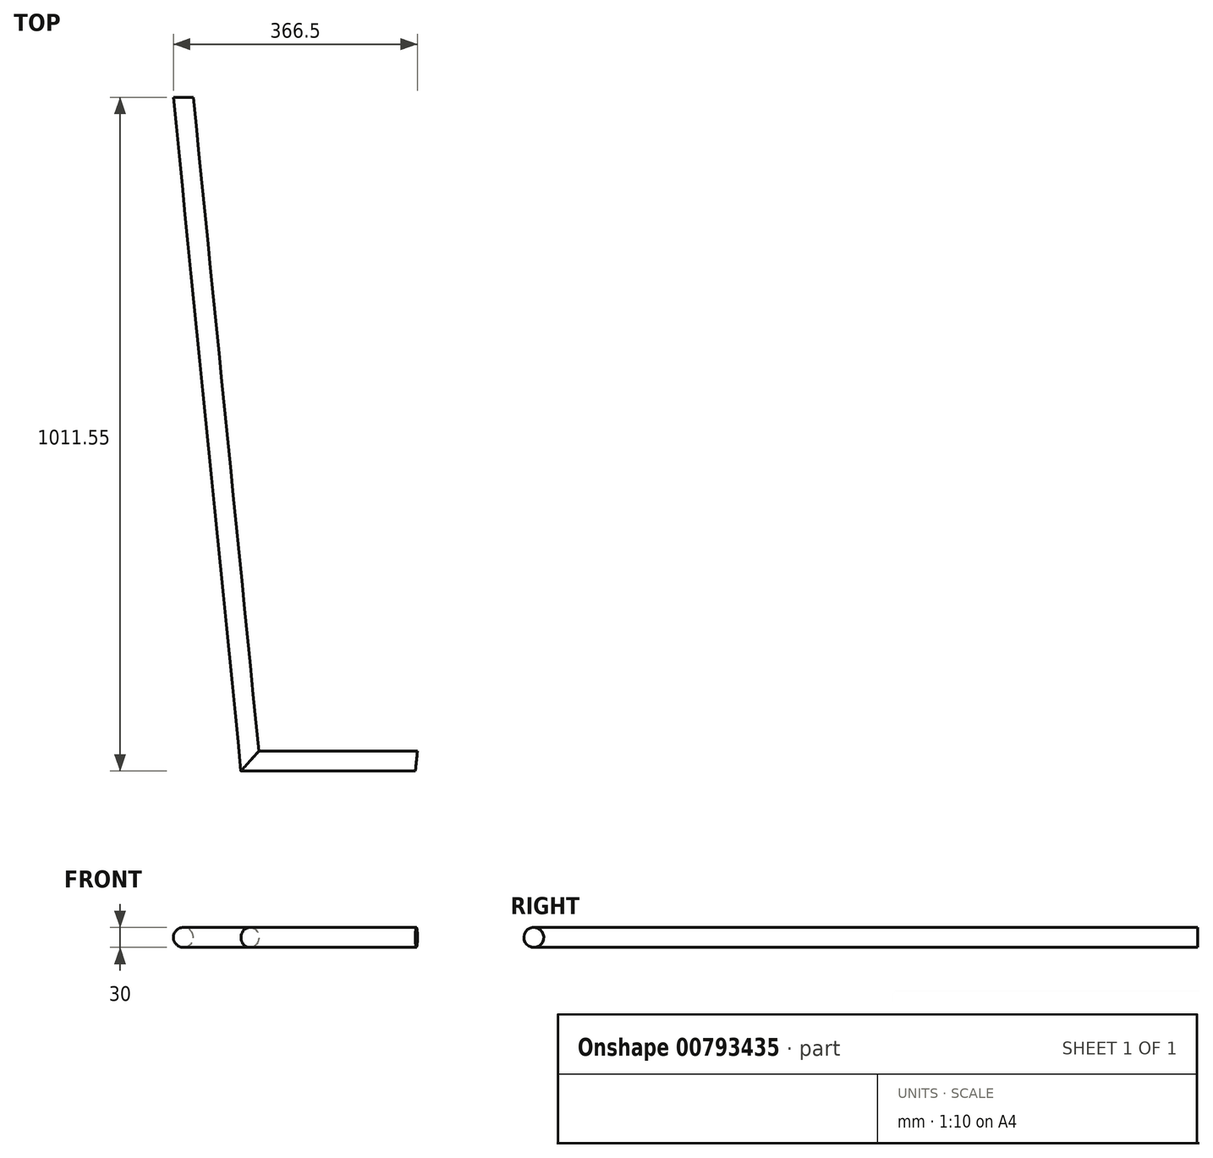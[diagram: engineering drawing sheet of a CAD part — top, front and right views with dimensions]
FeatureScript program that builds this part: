
annotation { "Feature Type Name" : "Feature", "Feature Type Description" : "" }
export const myFeature = defineFeature(function(context is Context, id is Id, definition is map)
    precondition{}
    {
        {
            var Q0;
            Q0=qCreatedBy(makeId("Top.planeOp"),FACE);
            var sketch = newSketch(context, id + "F0", { "sketchPlane" : qUnion([Q0])});
            skLineSegment(sketch, "E0", {"start": v(0, 0) * mm, "end": v(-250, 0) * mm});
            skLineSegment(sketch, "E1", {"start": v(0, -996.63) * mm, "end": v(100, -996.63) * mm});
            skLineSegment(sketch, "E2", {"start": v(100, -996.63) * mm, "end": v(0, 0) * mm});
            skLineSegment(sketch, "E3", {"start": v(100, -996.63) * mm, "end": v(350, -996.63) * mm});
            skLineSegment(sketch, "E4", {"start": v(0, 0) * mm, "end": v(400, 0) * mm});
            skSolve(sketch);
        }
        {
            var Q0;
            Q0=qCreatedBy(makeId("Front.planeOp"),FACE);
            var sketch = newSketch(context, id + "F1", { "sketchPlane" : qUnion([Q0])});
            skCircle(sketch, "E5", {"center": v(0, 0) * mm, "radius": 15 * mm});
            skSolve(sketch);
        }
        {
            var Q0;
            Q0=makeQuery(id+"F1.imprint","IMPRINT",FACE,{"disambiguationData":[TD([[makeQuery(id+"F1.imprint","IMPRINT",EDGE,{"derivedFrom":sQuery(id+"F1.wireOp",EDGE,"E5")}),1.0]])]});
            var Q1;
            Q1=sQuery(id+"F0.wireOp",EDGE,"E2");
            var Q2;
            Q2=sQuery(id+"F0.wireOp",EDGE,"E3");
            sweep(context, id + "F2", {"profiles" : qUnion([Q0]), "path" : qUnion([Q1, Q2])});
        }
    });
